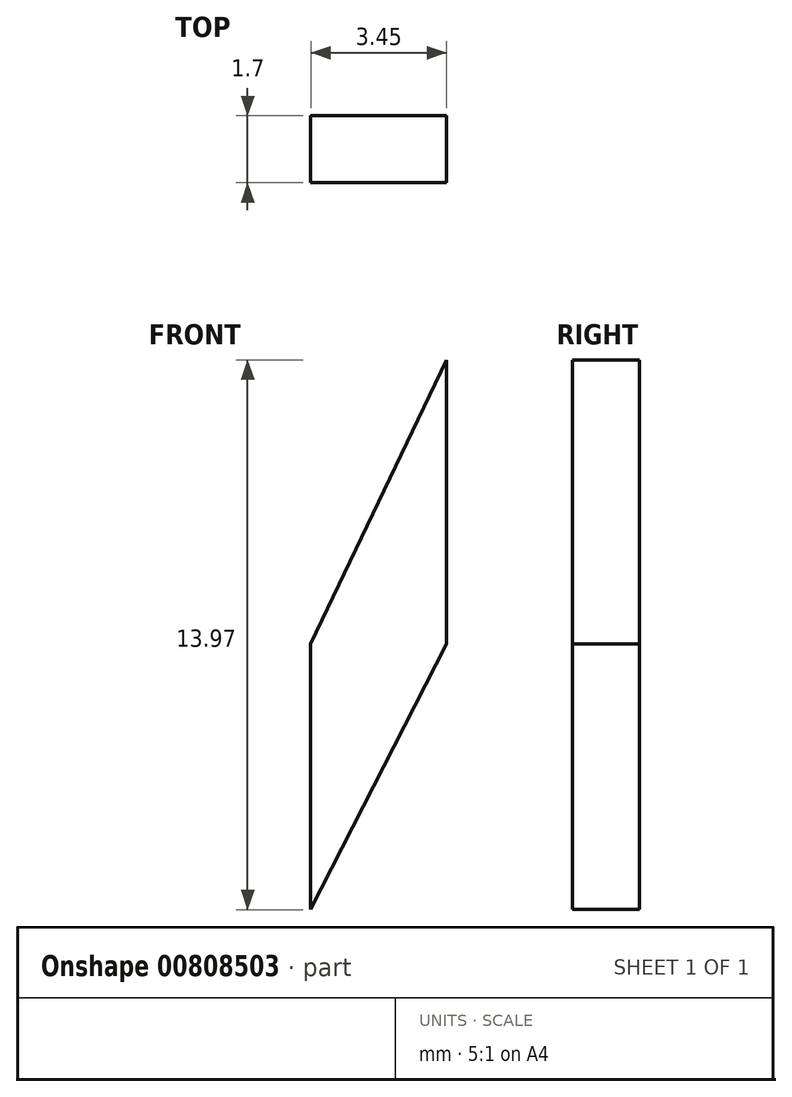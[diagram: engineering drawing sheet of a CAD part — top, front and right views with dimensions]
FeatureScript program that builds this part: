
annotation { "Feature Type Name" : "Feature", "Feature Type Description" : "" }
export const myFeature = defineFeature(function(context is Context, id is Id, definition is map)
    precondition{}
    {
        {
            var Q0;
            Q0=qCreatedBy(makeId("Front.planeOp"),FACE);
            var sketch = newSketch(context, id + "F0", { "sketchPlane" : qUnion([Q0])});
            skLineSegment(sketch, "E0", {"start": v(-55.12, 11.45) * mm, "end": v(-55.12, 18.2) * mm});
            skLineSegment(sketch, "E1", {"start": v(-55.12, 18.2) * mm, "end": v(-51.67, 25.42) * mm});
            skLineSegment(sketch, "E2", {"start": v(-51.67, 25.42) * mm, "end": v(-51.67, 18.2) * mm});
            skLineSegment(sketch, "E3", {"start": v(-51.67, 18.2) * mm, "end": v(-55.12, 11.45) * mm});
            skSolve(sketch);
        }
        {
            var Q0;
            Q0=makeQuery(id+"F0.imprint","IMPRINT",FACE,{"disambiguationData":[TD([[makeQuery(id+"F0.imprint","IMPRINT",EDGE,{"derivedFrom":sQuery(id+"F0.wireOp",EDGE,"E0")}),-1.0]])]});
            extrude(context, id + "F1", {"entities" : qUnion([Q0]), "depth" : 1.7 * mm, "offsetDistance" : 25.4 * mm});
        }
    });
